# Revit family: Urinals-Commercial_High-Efficiency_UT105U_TOTO
name_source: partatom
category: Plumbing Fixtures
revit_build: Autodesk Revit Architecture 2013 (Build: 20130531_2115(x64)
units: mm (PartAtom-declared; Revit-internal decimal feet)

## types (2) — shared parameters
04 CSI = 22 42 13
95 CSI = 15410
ADA Compliant = Yes
Assembly Code = D2010210
CAD Drawing URL = http://assets.totousa.com
CW Connection = Yes
Certifications = IAPMO(cUPC), State of Massachusetts, City of Los Angeles
Code Compliance = UPC, IPC, NSPC, NPC Canada, and others
Cold Water Connection Diameter = 0' - 2"
Cold Water Connection NPT Radius = 3/8"
Cold Water Connection Radius = 0' - 1"
Cold Water Connector = Cold Water Connection
Color Availability = #01 Cotton, #03 Bone, #12 Sedona Beige
Default Elevation = 0' - 0"
Depth = 1' - 2"
Finish = Vitreous China - TOTO - 01 Cotton
Flush Valve Model = Flush Valve Model : TEU1UN12
Gallons Per Flush = 0.125 gal
HW Connection = No
Industry Standards = Meets and exceeds ASME A112.19.2/CSA B45.1
Manufacturer = TOTO USA, Inc.
Manufacturer Fax = (770) 282-0002
Material = Vitreous China
Mount Type = Wall
Sanitary Connector = Sanitary Connection
Shipping Weight = 37.50 lb
Spec Sheet URL = http://assets.totousa.com
Style = Commercial
Subcategory = Urinals
Toto BIM Number = BM-00240
URL = http://www.totousa.com
Vent Connection = Yes
Warranty = One Year Limited Warranty
Warranty URL = http://www.totousa.com
Waste Connection = Yes
Waste Connection NPT Radius = 0' - 1"
Width = 1' - 0 1/4"
zero-valued in all types: CWFU, HWFU, WFU

## per-type parameters (varying)
| type | Available in SanoGloss | Description | Height |
| UT105U | No | Commercial Washout High-Efficiency Urinal, 1/8 GPF - ADA | 1' - 9 3/4" |
| UT105UG | Yes | Commercial Washout High-Efficiency Urinal, 1/8 GPF - ADA - SanaGloss® | 1' - 9 1/4" |

note: column(s) folded — value = type name in every type: Model

## geometry (parser evidence)
native form markers: Blend x6, Sweep x7
no freeform markers — native parametric forms only
